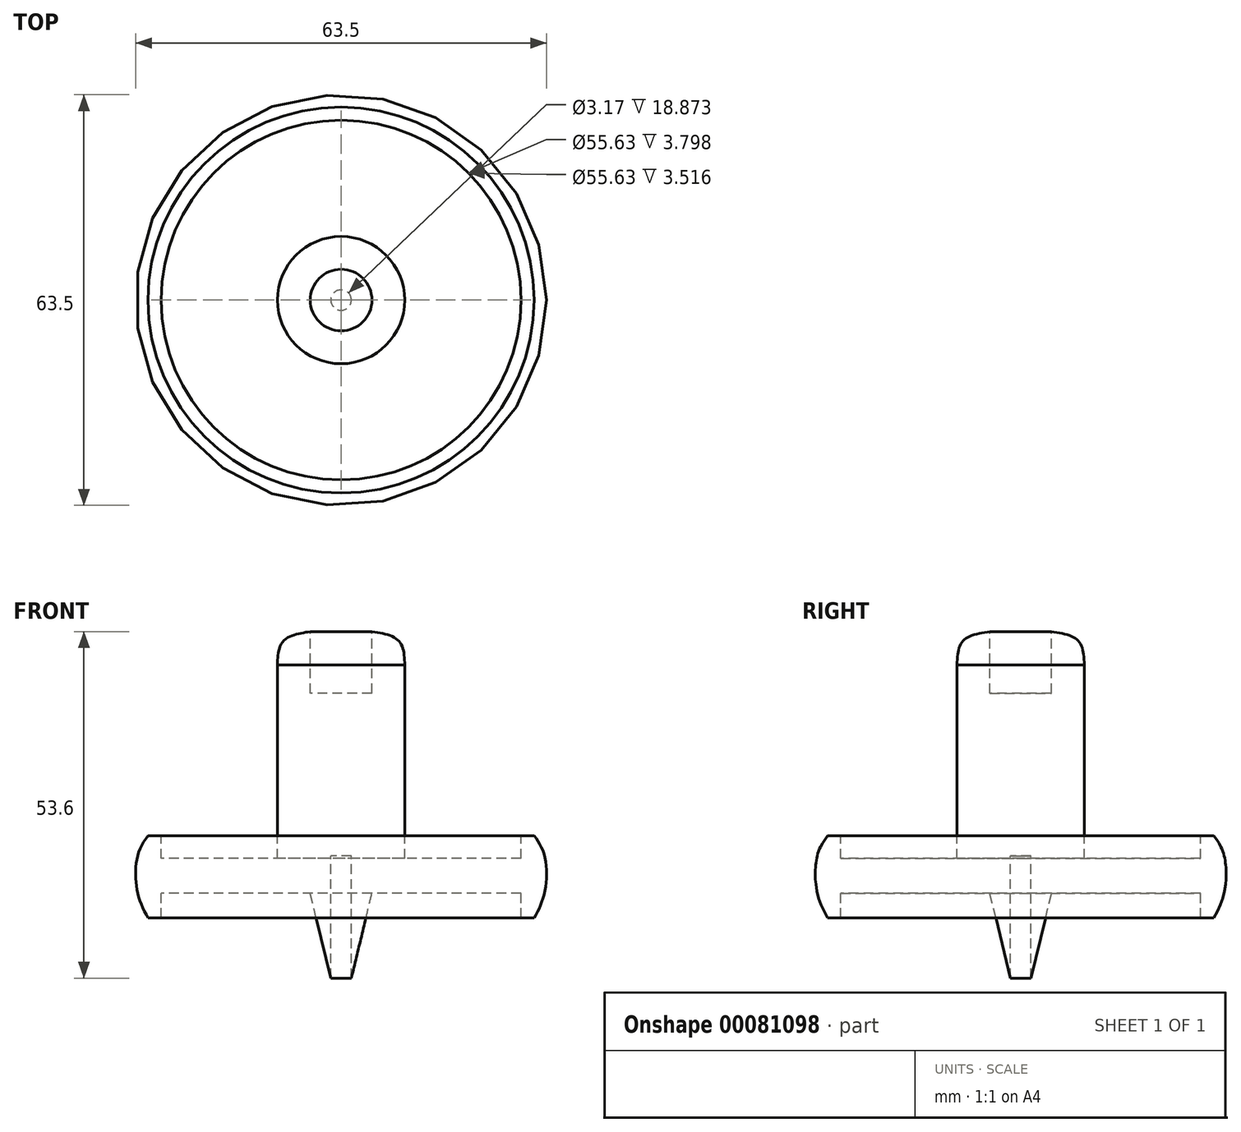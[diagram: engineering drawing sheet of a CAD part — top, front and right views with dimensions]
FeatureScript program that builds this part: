
annotation { "Feature Type Name" : "Feature", "Feature Type Description" : "" }
export const myFeature = defineFeature(function(context is Context, id is Id, definition is map)
    precondition{}
    {
        {
            var Q0;
            Q0=qCreatedBy(makeId("Front.planeOp"),FACE);
            var sketch = newSketch(context, id + "F0", { "sketchPlane" : qUnion([Q0])});
            skLineSegment(sketch, "E0", {"start": v(4.76, 49.6) * mm, "end": v(4.76, 40.08) * mm});
            skLineSegment(sketch, "E1", {"start": v(4.76, 40.08) * mm, "end": v(0, 40.08) * mm});
            skLineSegment(sketch, "E2", {"start": v(29.84, 18.02) * mm, "end": v(29.84, 5.32) * mm});
            skLineSegment(sketch, "E3", {"start": v(4.76, 40.08) * mm, "end": v(4.76, 11.8) * mm});
            skLineSegment(sketch, "E4", {"start": v(29.84, 14.5) * mm, "end": v(29.84, 11.8) * mm});
            skLineSegment(sketch, "E5", {"start": v(29.84, 11.8) * mm, "end": v(29.84, 9.12) * mm});
            skLineSegment(sketch, "E6", {"start": v(29.84, 14.5) * mm, "end": v(4.76, 14.5) * mm});
            skLineSegment(sketch, "E7", {"start": v(29.84, 9.12) * mm, "end": v(4.76, 9.12) * mm});
            skFitSpline(sketch, "E8", {"points": [v(9.84, 44.46) * mm, v(8.96, 48.1) * mm, v(4.76, 49.6) * mm], "startDerivative": vector(-0.37, 8.77) * mm, "endDerivative": vector(-9.66, 1.62) * mm});
            skLineSegment(sketch, "E9", {"start": v(9.84, 44.46) * mm, "end": v(9.84, 14.5) * mm});
            skFitSpline(sketch, "E10", {"points": [v(29.84, 5.32) * mm, v(31.1, 7.98) * mm, v(31.75, 11.8) * mm, v(31.22, 15.67) * mm, v(29.84, 18.02) * mm], "startDerivative": vector(5.85, 10.7) * mm, "endDerivative": vector(-6.84, 9.53) * mm});
            skLineSegment(sketch, "E11", {"start": v(29.84, 18.02) * mm, "end": v(27.81, 18.02) * mm});
            skLineSegment(sketch, "E12", {"start": v(27.81, 18.02) * mm, "end": v(27.81, 5.32) * mm});
            skLineSegment(sketch, "E13", {"start": v(27.81, 5.32) * mm, "end": v(29.84, 5.32) * mm});
            skLineSegment(sketch, "E14", {"start": v(1.59, -3.99) * mm, "end": v(4.76, 9.12) * mm});
            skLineSegment(sketch, "E15", {"start": v(1.59, -3.99) * mm, "end": v(1.59, 14.89) * mm});
            skLineSegment(sketch, "E16", {"start": v(1.59, 14.89) * mm, "end": v(0, 14.89) * mm});
            skLineSegment(sketch, "E17", {"start": v(0, 40.08) * mm, "end": v(0, 14.89) * mm});
            skSolve(sketch);
        }
        {
            var Q0;
            Q0 = qSketchRegion(id + "F0", true);
            var Q1;
            Q1=sQuery(id+"F0.wireOp",EDGE,"E17");
            revolve(context, id + "F1", {"entities" : qUnion([Q0]), "axis" : qUnion([Q1]), "revolveType" : RevolveType.FULL});
        }
    });
